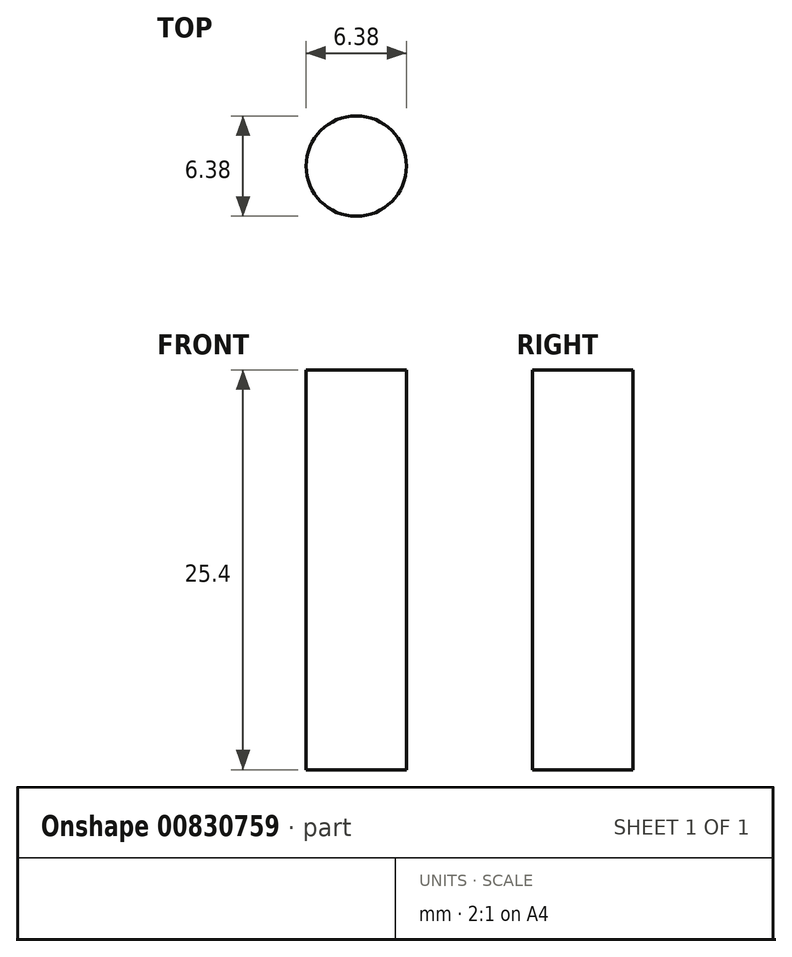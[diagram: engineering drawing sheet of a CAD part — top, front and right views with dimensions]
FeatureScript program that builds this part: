
annotation { "Feature Type Name" : "Feature", "Feature Type Description" : "" }
export const myFeature = defineFeature(function(context is Context, id is Id, definition is map)
    precondition{}
    {
        {
            var Q0;
            Q0=qCreatedBy(makeId("Top.planeOp"),FACE);
            var sketch = newSketch(context, id + "F0", { "sketchPlane" : qUnion([Q0])});
            skCircle(sketch, "E0", {"center": v(0, 0) * mm, "radius": 3.2 * mm});
            skSolve(sketch);
        }
        {
            var Q0;
            Q0 = qSketchRegion(id + "F0", true);
            extrude(context, id + "F1", {"entities" : qUnion([Q0]), "oppositeDirection" : true, "depth" : 25.4 * mm, "offsetDistance" : 25.4 * mm});
        }
    });
